# Revit family: RRHDWSUB
name_source: partatom
category: Generic Models
revit_build: Autodesk Revit 2018 (Build: 20190510_1515(x64)
units: mm (PartAtom-declared; Revit-internal decimal feet)

## family parameters
Always vertical = No
Can host rebar = No
Cut with Voids When Loaded = No
Part Type = Normal
Room Calculation Point = No
Round Connector Dimension = Use Diameter
Shared = Yes
Work Plane-Based = Yes

## types (10) — shared parameters
Default Elevation = 48 "

## per-type parameters (varying)
| type | Description | Inside Diameter | Inside Radius | U Radius | UBolt Length | Width |
| RRHDWSUBSCPNT1/2 | U-Bolt 1/2 Inch Hygienic w/ Beveled 3/8-16 Cap Nuts 316 | 1 " | 0.5 " | 0.69 " | 1.69 " | 1.38 " |
| RRHDWSUBSCPNT3/4 | U-Bolt 3/4 Inch Hygienic w/ Beveled 3/8-16 Cap Nuts 316 | 1.25 " | 0.625 " | 0.815 " | 1.88 " | 1.63 " |
| RRHDWSUBSCPNT1 | U-Bolt 1 Inch Hygienic w/ Beveled 3/8-16 Cap Nuts 316 | 1.5 " | 0.75 " | 0.94 " | 2.12 " | 1.88 " |
| RRHDWSUBSCPNT1-1/4 | U-Bolt 1 1/4 Inch Hygienic w/ Beveled 3/8-16 Cap Nuts 316 | 1.75 " | 0.875 " | 1.065 " | 2.5 " | 2.13 " |
| RRHDWSUBSCPNT1-1/2 | U-Bolt 1 1/2 Inch Hygienic w/ Beveled 3/8-16 Cap Nuts 316 | 2 " | 1 " | 1.19 " | 2.75 " | 2.38 " |
| RRHDWSUBSCPNT2 | U-Bolt 2 Inch Hygienic w/ Beveled 3/8-16 Cap Nuts 316 | 2.5 " | 1.25 " | 1.44 " | 3.25 " | 2.88 " |
| RRHDWSUBSCPNT2-1/2 | U-Bolt 2 1/2 Inch Hygienic w/ Beveled 3/8-16 Cap Nuts 316 | 3 " | 1.5 " | 1.69 " | 3.69 " | 3.38 " |
| RRHDWSUBSCPNT3 | U-Bolt 3 Inch Hygienic w/ Beveled 3/8-16 Cap Nuts 316 | 3.5 " | 1.75 " | 1.94 " | 4.31 " | 3.88 " |
| RRHDWSUBSCPNT4 | U-Bolt 4 Inch Hygienic w/ Beveled 3/8-16 Cap Nuts 316 | 4.56 " | 2.28 " | 2.47 " | 5.31 " | 4.94 " |
| RRHDWSUBEXARM2 | U-Bolt Post Mount 2 Inch Hygienic w/ Beveled 3/8-16 Cap Nuts 316 | 2.5 " | 1.25 " | 1.44 " | 2.88 " | 2.88 " |

note: column(s) folded — value = type name in every type: Catalog Number

## geometry (parser evidence)
native form markers: Sweep x7
no freeform markers — native parametric forms only
